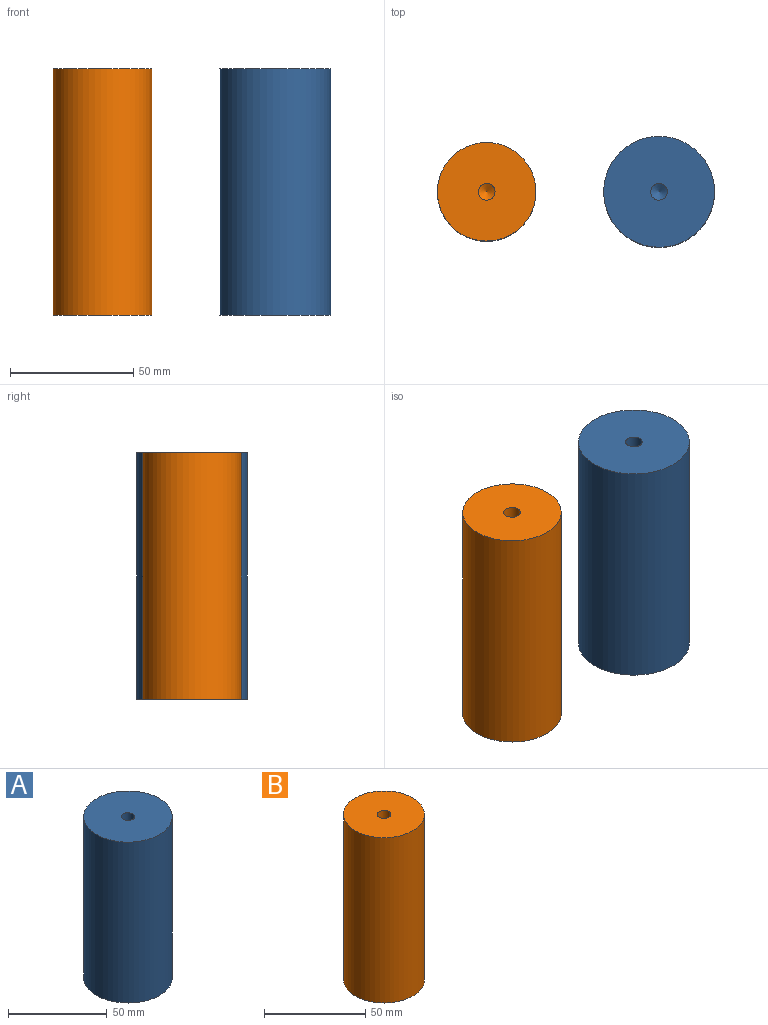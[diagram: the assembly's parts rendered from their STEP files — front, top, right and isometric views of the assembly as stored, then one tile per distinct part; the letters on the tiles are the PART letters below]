
ASSEMBLY  parts=2 mates=1
PART A: 7 faces, bbox 45x45x100 mm
  f0: cylinder r=22.5mm len=100mm, axis (0,0,-1), area 14137.2mm2, adj f1,f2
  f1: plane 45x45mm, normal (0,0,1), area 1554.1mm2, adj f0,f4
  f2: plane 45x45mm, normal (0,0,-1), area 1554.1mm2, adj f0,f6
  f3: cone r=0mm half-angle=59deg, axis (0,0,1), area 42.4mm2, adj f4
  f4: cylinder r=3.4mm len=23.75mm, axis (0,0,1), area 507.4mm2, adj f1,f3
  f5: cone r=0mm half-angle=59deg, axis (0,0,-1), area 42.4mm2, adj f6
  f6: cylinder r=3.4mm len=23.75mm, axis (0,0,-1), area 507.4mm2, adj f2,f5
PART B: 7 faces, bbox 40x40x100 mm
  f0: cylinder r=20mm len=100mm, axis (0,0,-1), area 12566.4mm2, adj f1,f2
  f1: plane 40x40mm, normal (0,0,1), area 1220.3mm2, adj f0,f4
  f2: plane 40x40mm, normal (0,0,-1), area 1220.3mm2, adj f0,f6
  f3: cone r=0mm half-angle=59deg, axis (0,0,1), area 42.4mm2, adj f4
  f4: cylinder r=3.4mm len=23.75mm, axis (0,0,1), area 507.4mm2, adj f1,f3
  f5: cone r=0mm half-angle=59deg, axis (0,0,-1), area 42.4mm2, adj f6
  f6: cylinder r=3.4mm len=23.75mm, axis (0,0,-1), area 507.4mm2, adj f2,f5
PLACE A t=(-12.7,-41.15,0.94)mm
PLACE B t=(-82.7,-41.15,0.94)mm
MATE planar A.f0 <-> B.f0  axis (0,0,-1) through (-12.7,-41.15,-49.06)mm
